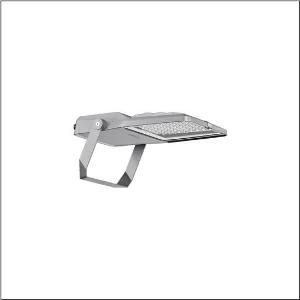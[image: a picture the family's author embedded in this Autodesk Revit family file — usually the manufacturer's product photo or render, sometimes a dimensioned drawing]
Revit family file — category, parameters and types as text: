
# Revit family: floodlight_fl_21_mini___pl43_5xa7775b2a1a_e8ea
name_source: partatom
category: Lighting Fixtures
units: mm (PartAtom-declared; Revit-internal decimal feet)

## family parameters
Cut with Voids When Loaded = No
Host = Face
Light Source = No
Part Type = Normal
Room Calculation Point = No
Round Connector Dimension = Use Diameter
Shared = No

## types (1)
- --- (1 x LED, 6390 lm, 45.7 W, 3000K)
    Apparent Load = 46 VA
    CIE Flux Codes = 27 78 99 100 100
    Color Rendering = 70
    Color Temperature = 3000K
    Default Elevation = 1800 mm
    Description = Floodlight FL 21 mini, floodlight, primary light control with lens, of PMMA, primary optical cover: protective disc, of toughened safety glass, transparent, light distribution: PL43, light emission: direct distribution, installation type: surface-mounted, LED, High Power LED, rated luminous flux: 6.390lm, luminous efficacy: 140lm/W, light colour: 730, colour temperature: 3000K, control: flexible luminous flux parameterisation, time-dependent luminous flux control, constant luminous flux control, overheat protection, presetting dimming logarithmic, with terminal, 6-pole, mains connection: 220..240V, AC, 50/60Hz, start of lifetime: 46W, end of service life: 48W, reduction: 22W, luminaire housing, of diecast aluminium, powder-coated, Siteco® metallic grey (DB 702S), corrosivity category C5 mid according to DIN EN ISO 12944, sealing non-destructively replaceable, mounting bracket, of steel, galvanised, powder-coated, Siteco® metallic grey (DB 702S), Smart Interface above, protection rating (complete): IP66, insulation class (complete): insulation class II (safety insulation), certification: CE, ENEC, VDE, protection symbol: D, impact resistance: IK08, permissible operating ambient temperature: -40..+40°C, permissible operating ambient temperature for outdoor applications: -40..+50°C, standard: DIN EN 12944, LABS conformity tested according to VDMA 24364:2018-05, packaging unit: 1 piece

Light Distribution: PL43
    Height = 70 mm
    Lamp = 1 x LED
    Lamp Light Flux = 6390 lm
    Lamp Power = 45.7 W
    Lamp count = 1
    Length = 485 mm
    Luminous efficacy = 140 lm/W
    Manufacturer = Siteco
    ModVariant = No
    Model = 5XA7775B2A1A
    Number of Poles = 1
    OnlyDefault = Yes
    Power Factor = 1
    Product Name = Floodlight FL 21 mini | PL43
    Product group = floodlight | pylon annexe
    ProductGroupID = 6200
    Protection Class = Protection class II
    Protection Degree = IP 66
    RLX_Detail_Level = 1
    RLX_Emergency_Light_Flux = 0 lm
    RLX_Emergency_Type = 0
    RLX_Emergency_Type_DB = No
    RlxData = <blob elided: 95873 chars, md5=3871b73a>
    Socket = socket
    Standby Power = 0 W
    System Light Flux = 6390 lm
    System Power = 46 W
    Type Comments = factory setting: luminous flux: 100 % | dim-lin: 254 | 463 mA
    Type Image = l_1006845.jpg
    URL = http://relux.com
    VarID = @adj_093625
    Voltage = 0 V
    Weight = 0.00 kg
    Width = 337 mm

## geometry (parser evidence)
native form markers: Blend x4, Sweep x12
no freeform markers — native parametric forms only
